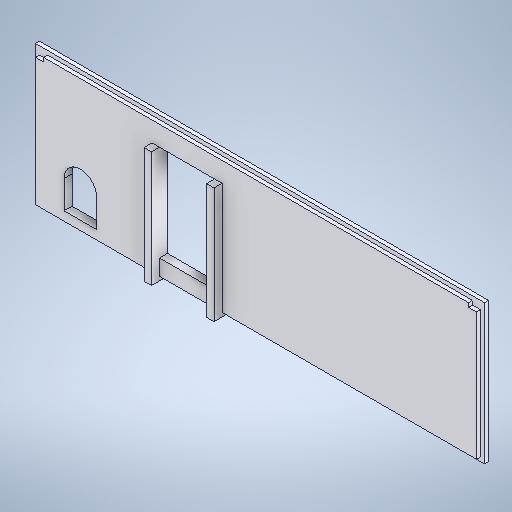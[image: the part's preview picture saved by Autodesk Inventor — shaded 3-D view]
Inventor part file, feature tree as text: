
AUTODESK INVENTOR PART (.ipt)
format: ipt  version: 2025 (Build 290162000, 162)  size: 328,192 bytes
history: native  units: in
note: dims shown in document units (in); Inventor stores cm internally (conversion verified against a paired STEP export)
features: extrude x7, sketch x7, projected_geometry x6
ambient origin geometry x8: Origin, YZ Plane, XZ Plane, XY Plane, X Axis, Y Axis, Z Axis, Center Point
bodies: Solid1 (feature_tree)
feature tree (20):
  extrude  "Extrusion1"  Depth=2.75in
  extrude  "Extrusion2"  Depth=0.0787in
  extrude  "Extrusion3"  Depth=0.1575in
  extrude  "Extrusion4"  Depth=0.1575in
  extrude  "Extrusion5"  Depth=0.0787in TaperAngle=0.0deg
  extrude  "Extrusion6"  Depth=0.4528in
  extrude  "Extrusion7"  Depth=0.3937in
  sketch  "Sketch1"  dims[d0=8.8425in d1=2.75in]
  sketch  "Sketch2"  dims[d2=0.0787in d3=0.0in d4=0.0787in]
  projected_geometry  "Projected Loop1"
  sketch  "Sketch3"  dims[d5=0.0787in d6=0.0in d7=0.1575in]
  projected_geometry  "Projected Loop2"
  sketch  "Sketch4"  dims[d8=0.0787in d9=0.1575in]
  projected_geometry  "Projected Loop3"
  sketch  "Sketch5"  dims[d10=0.0787in d11=0.0787in d12=0.0in]
  projected_geometry  "Projected Loop4"
  sketch  "Sketch6"  dims[d13=0.8957in d14=0.4528in]
  projected_geometry  "Projected Loop5"
  sketch  "Sketch7"  dims[d15=0.6398in d16=0.5512in d17=0.3937in d18=0.0in d19=1.7815in d20=1.0827in d21=1.8898in d22=0.3937in d23=0.0in d24=0.1476in d25=0.1476in d26=0.1575in d27=0.0787in d28=0.0in d29=0.0in d30=0.3199in d31=0.3937in d32=0.0in]
  projected_geometry  "Projected Loop6"
